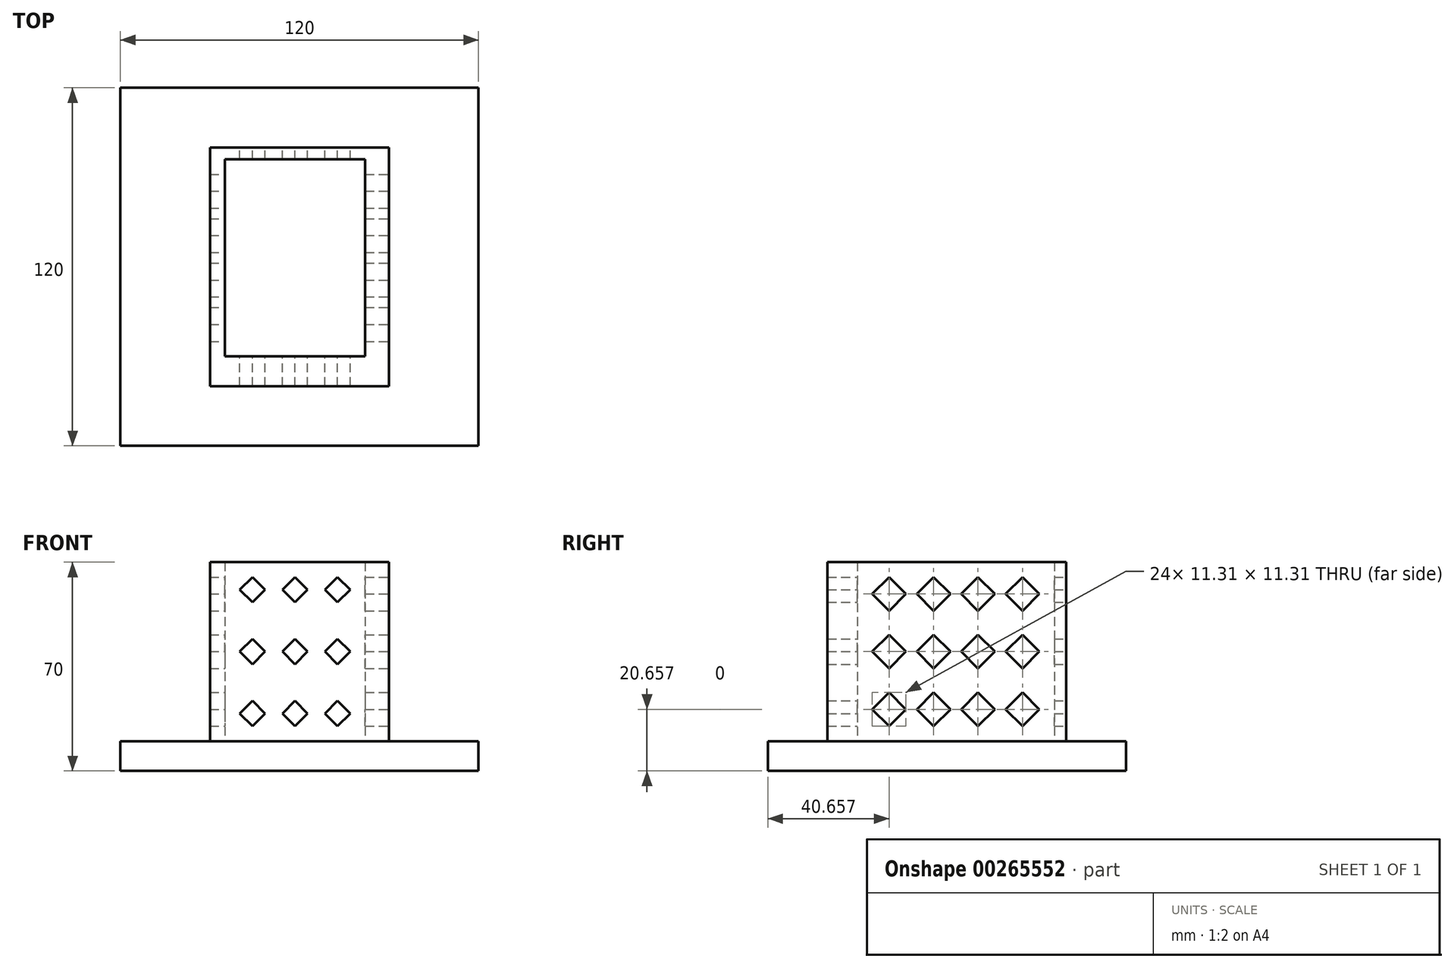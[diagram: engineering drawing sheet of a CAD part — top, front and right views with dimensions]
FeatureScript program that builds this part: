
annotation { "Feature Type Name" : "Feature", "Feature Type Description" : "" }
export const myFeature = defineFeature(function(context is Context, id is Id, definition is map)
    precondition{}
    {
        {
            var Q0;
            Q0=qCreatedBy(makeId("Top.planeOp"),FACE);
            var sketch = newSketch(context, id + "F0", { "sketchPlane" : qUnion([Q0])});
            skLineSegment(sketch, "E0.bottom", {"start": v(-30, -40) * mm, "end": v(30, -40) * mm});
            skLineSegment(sketch, "E0.top", {"start": v(-30, 40) * mm, "end": v(30, 40) * mm});
            skLineSegment(sketch, "E0.left", {"start": v(-30, -40) * mm, "end": v(-30, 40) * mm});
            skLineSegment(sketch, "E0.right", {"start": v(30, -40) * mm, "end": v(30, 40) * mm});
            skLineSegment(sketch, "E1.bottom", {"start": v(-25, 36) * mm, "end": v(22, 36) * mm});
            skLineSegment(sketch, "E1.top", {"start": v(-25, -30) * mm, "end": v(22, -30) * mm});
            skLineSegment(sketch, "E1.left", {"start": v(-25, 36) * mm, "end": v(-25, -30) * mm});
            skLineSegment(sketch, "E1.right", {"start": v(22, 36) * mm, "end": v(22, -30) * mm});
            skLineSegment(sketch, "E2", {"start": v(-30, 40) * mm, "end": v(30, -40) * mm, "construction": true});
            skSolve(sketch);
        }
        {
            var Q0;
            Q0 = qSketchRegion(id + "F0", true);
            extrude(context, id + "F1", {"entities" : qUnion([Q0]), "depth" : 60 * mm});
        }
        {
            var Q0;
            Q0=makeQuery(id+"F1.opExtrude","SWEPT_FACE",FACE,{"disambiguationData":[OSD([sQuery(id+"F0.wireOp",EDGE,"E0.right")])]});
            var sketch = newSketch(context, id + "F2", { "sketchPlane" : qUnion([Q0])});
            skLineSegment(sketch, "E3", {"start": v(-25, 49.34) * mm, "end": v(-19.34, 55) * mm});
            skLineSegment(sketch, "E4", {"start": v(-19.34, 55) * mm, "end": v(-13.69, 49.34) * mm});
            skLineSegment(sketch, "E5", {"start": v(-13.69, 49.34) * mm, "end": v(-19.34, 43.69) * mm});
            skLineSegment(sketch, "E6", {"start": v(-19.34, 43.69) * mm, "end": v(-25, 49.34) * mm});
            skLineSegment(sketch, "E7", {"start": v(-19.34, 55) * mm, "end": v(-19.34, 43.69) * mm, "construction": true});
            skLineSegment(sketch, "E8", {"start": v(-25, 49.34) * mm, "end": v(-13.69, 49.34) * mm, "construction": true});
            skLineSegment(sketch, "E9.0.1", {"start": v(-30, 0) * mm, "end": v(-30, 60) * mm});
            skLineSegment(sketch, "E9.0.3", {"start": v(-30, 60) * mm, "end": v(-30, 0) * mm});
            skLineSegment(sketch, "E10.1.0.0", {"start": v(-10.1, 49.34) * mm, "end": v(-4.45, 55) * mm});
            skLineSegment(sketch, "E10.1.0.1", {"start": v(-4.45, 55) * mm, "end": v(1.2, 49.34) * mm});
            skLineSegment(sketch, "E10.1.0.2", {"start": v(1.2, 49.34) * mm, "end": v(-4.45, 43.69) * mm});
            skLineSegment(sketch, "E10.1.0.3", {"start": v(-4.45, 43.69) * mm, "end": v(-10.1, 49.34) * mm});
            skLineSegment(sketch, "E10.1.0.4", {"start": v(-4.45, 55) * mm, "end": v(-4.45, 43.69) * mm, "construction": true});
            skLineSegment(sketch, "E10.1.0.5", {"start": v(-10.1, 49.34) * mm, "end": v(1.2, 49.34) * mm, "construction": true});
            skLineSegment(sketch, "E10.2.0.0", {"start": v(4.8, 49.34) * mm, "end": v(10.45, 55) * mm});
            skLineSegment(sketch, "E10.2.0.1", {"start": v(10.45, 55) * mm, "end": v(16.1, 49.34) * mm});
            skLineSegment(sketch, "E10.2.0.2", {"start": v(16.1, 49.34) * mm, "end": v(10.45, 43.69) * mm});
            skLineSegment(sketch, "E10.2.0.3", {"start": v(10.45, 43.69) * mm, "end": v(4.8, 49.34) * mm});
            skLineSegment(sketch, "E10.2.0.4", {"start": v(10.45, 55) * mm, "end": v(10.45, 43.69) * mm, "construction": true});
            skLineSegment(sketch, "E10.2.0.5", {"start": v(4.8, 49.34) * mm, "end": v(16.1, 49.34) * mm, "construction": true});
            skLineSegment(sketch, "E10.direction1", {"start": v(-19.34, 43.69) * mm, "end": v(-4.45, 43.69) * mm, "construction": true});
            skLineSegment(sketch, "E11.0.1", {"start": v(36, 0) * mm, "end": v(36, 60) * mm});
            skLineSegment(sketch, "E11.0.3", {"start": v(36, 60) * mm, "end": v(36, 0) * mm});
            skLineSegment(sketch, "E12.0.3.0", {"start": v(19.69, 49.34) * mm, "end": v(25.34, 55) * mm});
            skLineSegment(sketch, "E12.3.3.0", {"start": v(25.34, 55) * mm, "end": v(31, 49.34) * mm});
            skLineSegment(sketch, "E12.6.3.0", {"start": v(31, 49.34) * mm, "end": v(25.34, 43.69) * mm});
            skLineSegment(sketch, "E12.9.3.0", {"start": v(25.34, 43.69) * mm, "end": v(19.69, 49.34) * mm});
            skLineSegment(sketch, "E12.12.3.0", {"start": v(25.34, 55) * mm, "end": v(25.34, 43.69) * mm, "construction": true});
            skLineSegment(sketch, "E12.15.3.0", {"start": v(19.69, 49.34) * mm, "end": v(31, 49.34) * mm, "construction": true});
            skLineSegment(sketch, "E13.1.0.0", {"start": v(-4.45, 24.34) * mm, "end": v(-10.1, 30) * mm});
            skLineSegment(sketch, "E13.1.0.1", {"start": v(31, 30) * mm, "end": v(25.34, 24.34) * mm});
            skLineSegment(sketch, "E13.1.0.2", {"start": v(-4.45, 35.66) * mm, "end": v(-4.45, 24.34) * mm, "construction": true});
            skLineSegment(sketch, "E13.1.0.3", {"start": v(-10.1, 30) * mm, "end": v(-4.45, 35.66) * mm});
            skLineSegment(sketch, "E13.1.0.4", {"start": v(-25, 30) * mm, "end": v(-13.69, 30) * mm, "construction": true});
            skLineSegment(sketch, "E13.1.0.5", {"start": v(-25, 30) * mm, "end": v(-19.34, 35.66) * mm});
            skLineSegment(sketch, "E13.1.0.6", {"start": v(4.8, 30) * mm, "end": v(10.45, 35.66) * mm});
            skLineSegment(sketch, "E13.1.0.7", {"start": v(4.8, 30) * mm, "end": v(16.1, 30) * mm, "construction": true});
            skLineSegment(sketch, "E13.1.0.8", {"start": v(25.34, 24.34) * mm, "end": v(19.69, 30) * mm});
            skLineSegment(sketch, "E13.1.0.9", {"start": v(10.45, 35.66) * mm, "end": v(10.45, 24.34) * mm, "construction": true});
            skLineSegment(sketch, "E13.1.0.10", {"start": v(-19.34, 35.66) * mm, "end": v(-13.69, 30) * mm});
            skLineSegment(sketch, "E13.1.0.11", {"start": v(10.45, 35.66) * mm, "end": v(16.1, 30) * mm});
            skLineSegment(sketch, "E13.1.0.12", {"start": v(1.2, 30) * mm, "end": v(-4.45, 24.34) * mm});
            skLineSegment(sketch, "E13.1.0.13", {"start": v(-10.1, 30) * mm, "end": v(1.2, 30) * mm, "construction": true});
            skLineSegment(sketch, "E13.1.0.14", {"start": v(-4.45, 35.66) * mm, "end": v(1.2, 30) * mm});
            skLineSegment(sketch, "E13.1.0.15", {"start": v(10.45, 24.34) * mm, "end": v(4.8, 30) * mm});
            skLineSegment(sketch, "E13.1.0.16", {"start": v(-19.34, 35.66) * mm, "end": v(-19.34, 24.34) * mm, "construction": true});
            skLineSegment(sketch, "E13.1.0.17", {"start": v(25.34, 35.66) * mm, "end": v(31, 30) * mm});
            skLineSegment(sketch, "E13.1.0.18", {"start": v(19.69, 30) * mm, "end": v(31, 30) * mm, "construction": true});
            skLineSegment(sketch, "E13.1.0.19", {"start": v(-19.34, 24.34) * mm, "end": v(-25, 30) * mm});
            skLineSegment(sketch, "E13.1.0.20", {"start": v(-13.69, 30) * mm, "end": v(-19.34, 24.34) * mm});
            skLineSegment(sketch, "E13.1.0.21", {"start": v(16.1, 30) * mm, "end": v(10.45, 24.34) * mm});
            skLineSegment(sketch, "E13.1.0.22", {"start": v(-19.34, 24.34) * mm, "end": v(-4.45, 24.34) * mm, "construction": true});
            skLineSegment(sketch, "E13.1.0.23", {"start": v(19.69, 30) * mm, "end": v(25.34, 35.66) * mm});
            skLineSegment(sketch, "E13.1.0.24", {"start": v(25.34, 35.66) * mm, "end": v(25.34, 24.34) * mm, "construction": true});
            skLineSegment(sketch, "E13.2.0.0", {"start": v(-4.45, 5) * mm, "end": v(-10.1, 10.66) * mm});
            skLineSegment(sketch, "E13.2.0.1", {"start": v(31, 10.66) * mm, "end": v(25.34, 5) * mm});
            skLineSegment(sketch, "E13.2.0.2", {"start": v(-4.45, 16.31) * mm, "end": v(-4.45, 5) * mm, "construction": true});
            skLineSegment(sketch, "E13.2.0.3", {"start": v(-10.1, 10.66) * mm, "end": v(-4.45, 16.31) * mm});
            skLineSegment(sketch, "E13.2.0.4", {"start": v(-25, 10.66) * mm, "end": v(-13.69, 10.66) * mm, "construction": true});
            skLineSegment(sketch, "E13.2.0.5", {"start": v(-25, 10.66) * mm, "end": v(-19.34, 16.31) * mm});
            skLineSegment(sketch, "E13.2.0.6", {"start": v(4.8, 10.66) * mm, "end": v(10.45, 16.31) * mm});
            skLineSegment(sketch, "E13.2.0.7", {"start": v(4.8, 10.66) * mm, "end": v(16.1, 10.66) * mm, "construction": true});
            skLineSegment(sketch, "E13.2.0.8", {"start": v(25.34, 5) * mm, "end": v(19.69, 10.66) * mm});
            skLineSegment(sketch, "E13.2.0.9", {"start": v(10.45, 16.31) * mm, "end": v(10.45, 5) * mm, "construction": true});
            skLineSegment(sketch, "E13.2.0.10", {"start": v(-19.34, 16.31) * mm, "end": v(-13.69, 10.66) * mm});
            skLineSegment(sketch, "E13.2.0.11", {"start": v(10.45, 16.31) * mm, "end": v(16.1, 10.66) * mm});
            skLineSegment(sketch, "E13.2.0.12", {"start": v(1.2, 10.66) * mm, "end": v(-4.45, 5) * mm});
            skLineSegment(sketch, "E13.2.0.13", {"start": v(-10.1, 10.66) * mm, "end": v(1.2, 10.66) * mm, "construction": true});
            skLineSegment(sketch, "E13.2.0.14", {"start": v(-4.45, 16.31) * mm, "end": v(1.2, 10.66) * mm});
            skLineSegment(sketch, "E13.2.0.15", {"start": v(10.45, 5) * mm, "end": v(4.8, 10.66) * mm});
            skLineSegment(sketch, "E13.2.0.16", {"start": v(-19.34, 16.31) * mm, "end": v(-19.34, 5) * mm, "construction": true});
            skLineSegment(sketch, "E13.2.0.17", {"start": v(25.34, 16.31) * mm, "end": v(31, 10.66) * mm});
            skLineSegment(sketch, "E13.2.0.18", {"start": v(19.69, 10.66) * mm, "end": v(31, 10.66) * mm, "construction": true});
            skLineSegment(sketch, "E13.2.0.19", {"start": v(-19.34, 5) * mm, "end": v(-25, 10.66) * mm});
            skLineSegment(sketch, "E13.2.0.20", {"start": v(-13.69, 10.66) * mm, "end": v(-19.34, 5) * mm});
            skLineSegment(sketch, "E13.2.0.21", {"start": v(16.1, 10.66) * mm, "end": v(10.45, 5) * mm});
            skLineSegment(sketch, "E13.2.0.22", {"start": v(-19.34, 5) * mm, "end": v(-4.45, 5) * mm, "construction": true});
            skLineSegment(sketch, "E13.2.0.23", {"start": v(19.69, 10.66) * mm, "end": v(25.34, 16.31) * mm});
            skLineSegment(sketch, "E13.2.0.24", {"start": v(25.34, 16.31) * mm, "end": v(25.34, 5) * mm, "construction": true});
            skLineSegment(sketch, "E13.direction1", {"start": v(-19.34, 43.69) * mm, "end": v(-19.34, 24.34) * mm, "construction": true});
            skSolve(sketch);
        }
        {
            var Q0;
            Q0 = qSketchRegion(id + "F2", true);
            extrude(context, id + "F3", {"entities" : qUnion([Q0]), "operationType" : NewBodyOperationType.REMOVE, "endBound" : BoundingType.THROUGH_ALL, "oppositeDirection" : true, "depth" : 25 * mm});
        }
        {
            var Q0;
            Q0=makeQuery(id+"F1.opExtrude","SWEPT_FACE",FACE,{"disambiguationData":[OSD([sQuery(id+"F0.wireOp",EDGE,"E0.top")])]});
            var sketch = newSketch(context, id + "F4", { "sketchPlane" : qUnion([Q0])});
            skLineSegment(sketch, "E14.0.1", {"start": v(-22, 0) * mm, "end": v(-22, 60) * mm});
            skLineSegment(sketch, "E14.0.3", {"start": v(-22, 60) * mm, "end": v(-22, 0) * mm});
            skLineSegment(sketch, "E15.0.1", {"start": v(25, 0) * mm, "end": v(25, 60) * mm});
            skLineSegment(sketch, "E15.0.3", {"start": v(25, 60) * mm, "end": v(25, 0) * mm});
            skLineSegment(sketch, "E16", {"start": v(-17, 50.76) * mm, "end": v(-12.76, 55) * mm});
            skLineSegment(sketch, "E17", {"start": v(-12.76, 55) * mm, "end": v(-8.51, 50.76) * mm});
            skLineSegment(sketch, "E18", {"start": v(-8.51, 50.76) * mm, "end": v(-12.76, 46.51) * mm});
            skLineSegment(sketch, "E19", {"start": v(-12.76, 46.51) * mm, "end": v(-17, 50.76) * mm});
            skLineSegment(sketch, "E20", {"start": v(-17, 50.76) * mm, "end": v(-8.51, 50.76) * mm, "construction": true});
            skLineSegment(sketch, "E21", {"start": v(-12.76, 55) * mm, "end": v(-12.76, 46.51) * mm, "construction": true});
            skLineSegment(sketch, "E22.0.1.0", {"start": v(-12.76, 34.24) * mm, "end": v(-8.51, 30) * mm});
            skLineSegment(sketch, "E22.0.1.1", {"start": v(-17, 30) * mm, "end": v(-12.76, 34.24) * mm});
            skLineSegment(sketch, "E22.0.1.2", {"start": v(-8.51, 30) * mm, "end": v(-12.76, 25.76) * mm});
            skLineSegment(sketch, "E22.0.1.3", {"start": v(-12.76, 34.24) * mm, "end": v(-12.76, 25.76) * mm, "construction": true});
            skLineSegment(sketch, "E22.0.1.4", {"start": v(-12.76, 25.76) * mm, "end": v(-17, 30) * mm});
            skLineSegment(sketch, "E22.0.1.5", {"start": v(-17, 30) * mm, "end": v(-8.51, 30) * mm, "construction": true});
            skLineSegment(sketch, "E22.0.2.0", {"start": v(-12.76, 13.49) * mm, "end": v(-8.51, 9.24) * mm});
            skLineSegment(sketch, "E22.0.2.1", {"start": v(-17, 9.24) * mm, "end": v(-12.76, 13.49) * mm});
            skLineSegment(sketch, "E22.0.2.2", {"start": v(-8.51, 9.24) * mm, "end": v(-12.76, 5) * mm});
            skLineSegment(sketch, "E22.0.2.3", {"start": v(-12.76, 13.49) * mm, "end": v(-12.76, 5) * mm, "construction": true});
            skLineSegment(sketch, "E22.0.2.4", {"start": v(-12.76, 5) * mm, "end": v(-17, 9.24) * mm});
            skLineSegment(sketch, "E22.0.2.5", {"start": v(-17, 9.24) * mm, "end": v(-8.51, 9.24) * mm, "construction": true});
            skLineSegment(sketch, "E22.1.0.0", {"start": v(1.5, 55) * mm, "end": v(5.74, 50.76) * mm});
            skLineSegment(sketch, "E22.1.0.1", {"start": v(-2.74, 50.76) * mm, "end": v(1.5, 55) * mm});
            skLineSegment(sketch, "E22.1.0.2", {"start": v(5.74, 50.76) * mm, "end": v(1.5, 46.51) * mm});
            skLineSegment(sketch, "E22.1.0.3", {"start": v(1.5, 55) * mm, "end": v(1.5, 46.51) * mm, "construction": true});
            skLineSegment(sketch, "E22.1.0.4", {"start": v(1.5, 46.51) * mm, "end": v(-2.74, 50.76) * mm});
            skLineSegment(sketch, "E22.1.0.5", {"start": v(-2.74, 50.76) * mm, "end": v(5.74, 50.76) * mm, "construction": true});
            skLineSegment(sketch, "E22.1.1.0", {"start": v(1.5, 34.24) * mm, "end": v(5.74, 30) * mm});
            skLineSegment(sketch, "E22.1.1.1", {"start": v(-2.74, 30) * mm, "end": v(1.5, 34.24) * mm});
            skLineSegment(sketch, "E22.1.1.2", {"start": v(5.74, 30) * mm, "end": v(1.5, 25.76) * mm});
            skLineSegment(sketch, "E22.1.1.3", {"start": v(1.5, 34.24) * mm, "end": v(1.5, 25.76) * mm, "construction": true});
            skLineSegment(sketch, "E22.1.1.4", {"start": v(1.5, 25.76) * mm, "end": v(-2.74, 30) * mm});
            skLineSegment(sketch, "E22.1.1.5", {"start": v(-2.74, 30) * mm, "end": v(5.74, 30) * mm, "construction": true});
            skLineSegment(sketch, "E22.1.2.0", {"start": v(1.5, 13.49) * mm, "end": v(5.74, 9.24) * mm});
            skLineSegment(sketch, "E22.1.2.1", {"start": v(-2.74, 9.24) * mm, "end": v(1.5, 13.49) * mm});
            skLineSegment(sketch, "E22.1.2.2", {"start": v(5.74, 9.24) * mm, "end": v(1.5, 5) * mm});
            skLineSegment(sketch, "E22.1.2.3", {"start": v(1.5, 13.49) * mm, "end": v(1.5, 5) * mm, "construction": true});
            skLineSegment(sketch, "E22.1.2.4", {"start": v(1.5, 5) * mm, "end": v(-2.74, 9.24) * mm});
            skLineSegment(sketch, "E22.1.2.5", {"start": v(-2.74, 9.24) * mm, "end": v(5.74, 9.24) * mm, "construction": true});
            skLineSegment(sketch, "E22.2.0.0", {"start": v(15.76, 55) * mm, "end": v(20, 50.76) * mm});
            skLineSegment(sketch, "E22.2.0.1", {"start": v(11.51, 50.76) * mm, "end": v(15.76, 55) * mm});
            skLineSegment(sketch, "E22.2.0.2", {"start": v(20, 50.76) * mm, "end": v(15.76, 46.51) * mm});
            skLineSegment(sketch, "E22.2.0.3", {"start": v(15.76, 55) * mm, "end": v(15.76, 46.51) * mm, "construction": true});
            skLineSegment(sketch, "E22.2.0.4", {"start": v(15.76, 46.51) * mm, "end": v(11.51, 50.76) * mm});
            skLineSegment(sketch, "E22.2.0.5", {"start": v(11.51, 50.76) * mm, "end": v(20, 50.76) * mm, "construction": true});
            skLineSegment(sketch, "E22.2.1.0", {"start": v(15.76, 34.24) * mm, "end": v(20, 30) * mm});
            skLineSegment(sketch, "E22.2.1.1", {"start": v(11.51, 30) * mm, "end": v(15.76, 34.24) * mm});
            skLineSegment(sketch, "E22.2.1.2", {"start": v(20, 30) * mm, "end": v(15.76, 25.76) * mm});
            skLineSegment(sketch, "E22.2.1.3", {"start": v(15.76, 34.24) * mm, "end": v(15.76, 25.76) * mm, "construction": true});
            skLineSegment(sketch, "E22.2.1.4", {"start": v(15.76, 25.76) * mm, "end": v(11.51, 30) * mm});
            skLineSegment(sketch, "E22.2.1.5", {"start": v(11.51, 30) * mm, "end": v(20, 30) * mm, "construction": true});
            skLineSegment(sketch, "E22.2.2.0", {"start": v(15.76, 13.49) * mm, "end": v(20, 9.24) * mm});
            skLineSegment(sketch, "E22.2.2.1", {"start": v(11.51, 9.24) * mm, "end": v(15.76, 13.49) * mm});
            skLineSegment(sketch, "E22.2.2.2", {"start": v(20, 9.24) * mm, "end": v(15.76, 5) * mm});
            skLineSegment(sketch, "E22.2.2.3", {"start": v(15.76, 13.49) * mm, "end": v(15.76, 5) * mm, "construction": true});
            skLineSegment(sketch, "E22.2.2.4", {"start": v(15.76, 5) * mm, "end": v(11.51, 9.24) * mm});
            skLineSegment(sketch, "E22.2.2.5", {"start": v(11.51, 9.24) * mm, "end": v(20, 9.24) * mm, "construction": true});
            skLineSegment(sketch, "E22.direction1", {"start": v(-12.76, 46.51) * mm, "end": v(1.5, 46.51) * mm, "construction": true});
            skLineSegment(sketch, "E22.direction2", {"start": v(-12.76, 46.51) * mm, "end": v(-12.76, 25.76) * mm, "construction": true});
            skSolve(sketch);
        }
        {
            var Q0;
            Q0 = qSketchRegion(id + "F4", true);
            extrude(context, id + "F5", {"entities" : qUnion([Q0]), "operationType" : NewBodyOperationType.REMOVE, "endBound" : BoundingType.THROUGH_ALL, "oppositeDirection" : true, "depth" : 25 * mm});
        }
        {
            var Q0;
            Q0=qCreatedBy(makeId("Top.planeOp"),FACE);
            var sketch = newSketch(context, id + "F6", { "sketchPlane" : qUnion([Q0])});
            skLineSegment(sketch, "E23.bottom", {"start": v(60, -60) * mm, "end": v(-60, -60) * mm});
            skLineSegment(sketch, "E23.top", {"start": v(60, 60) * mm, "end": v(-60, 60) * mm});
            skLineSegment(sketch, "E23.left", {"start": v(60, -60) * mm, "end": v(60, 60) * mm});
            skLineSegment(sketch, "E23.right", {"start": v(-60, -60) * mm, "end": v(-60, 60) * mm});
            skLineSegment(sketch, "E24", {"start": v(-60, 60) * mm, "end": v(60, -60) * mm});
            skLineSegment(sketch, "E25", {"start": v(60, 60) * mm, "end": v(-60, -60) * mm});
            skSolve(sketch);
        }
        {
            var Q0;
            Q0 = qSketchRegion(id + "F6", true);
            extrude(context, id + "F7", {"entities" : qUnion([Q0]), "operationType" : NewBodyOperationType.ADD, "oppositeDirection" : true, "depth" : 10 * mm});
        }
    });
